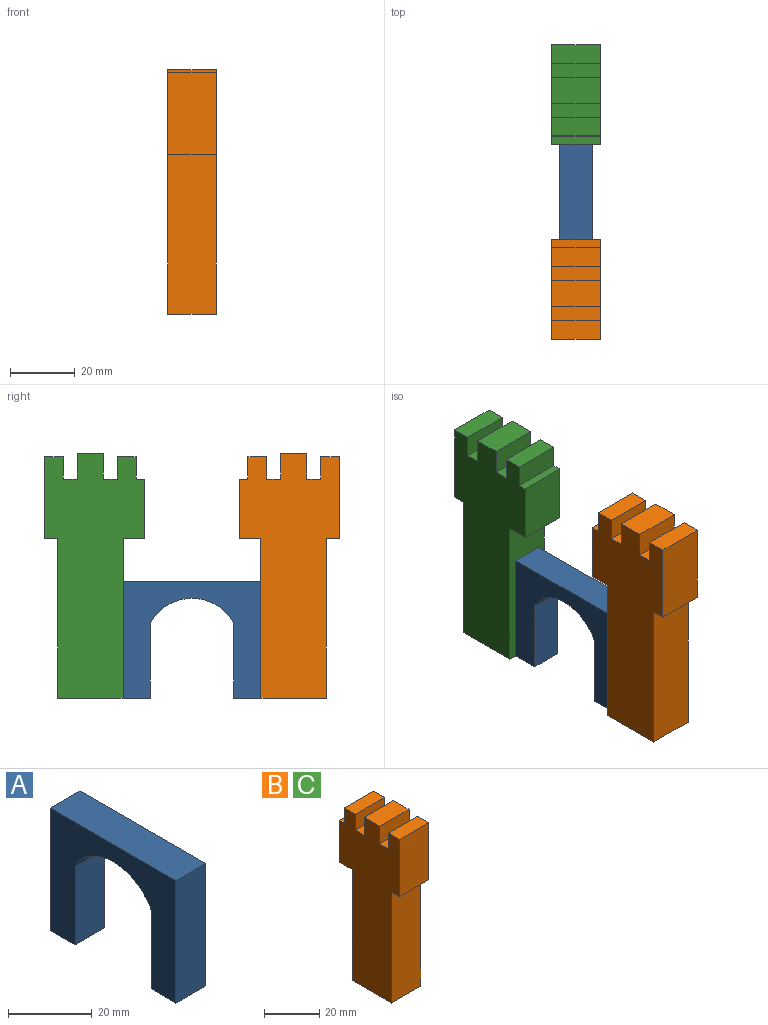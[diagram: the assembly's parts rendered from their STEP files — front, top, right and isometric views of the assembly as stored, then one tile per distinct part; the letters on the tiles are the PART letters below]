
ASSEMBLY  parts=3 mates=2
PART A: 10 faces, bbox 10x42.5x35.9 mm
  f0: plane 22.96x10mm, normal (0,-1,0), area 229.6mm2, adj f1,f7,f8,f9
  f1: plane 10x8.32mm, normal (0,0,-1), area 83.2mm2, adj f0,f2,f8,f9
  f2: plane 35.88x10mm, normal (0,1,0), area 358.8mm2, adj f1,f3,f8,f9
  f3: plane 42.48x10mm, normal (0,0,1), area 424.8mm2, adj f2,f4,f8,f9
  f4: plane 35.88x10mm, normal (0,-1,0), area 358.8mm2, adj f3,f5,f8,f9
  f5: plane 10x8.32mm, normal (0,0,-1), area 83.2mm2, adj f4,f6,f8,f9
  f6: plane 22.96x10mm, normal (0,1,0), area 229.6mm2, adj f5,f7,f8,f9
  f7: cylinder r=14.61mm len=25.83mm, axis (-1,0,0), area 316.8mm2, adj f0,f6,f8,f9
  f8: plane 42.48x35.88mm, normal (1,0,0), area 787.8mm2, adj f0,f1,f2,f3,f4,f5,f6,f7
  f9: plane 42.48x35.88mm, normal (-1,0,0), area 787.8mm2, adj f0,f1,f2,f3,f4,f5,f6,f7
PART B: 20 faces, bbox 15x30.7x75.2 mm
  f0: plane 49.08x15mm, normal (0,1,0), area 736.2mm2, adj f1,f17,f18,f19
  f1: plane 15x6.6mm, normal (0,0,-1), area 99mm2, adj f0,f2,f18,f19
  f2: plane 18.37x15mm, normal (0,1,0), area 275.5mm2, adj f1,f3,f18,f19
  f3: plane 15x2.58mm, normal (0,0,1), area 38.7mm2, adj f2,f4,f18,f19
  f4: plane 15x6.89mm, normal (0,1,0), area 103.3mm2, adj f3,f5,f18,f19
  f5: plane 15x5.74mm, normal (0,0,1), area 86.1mm2, adj f4,f6,f18,f19
  f6: plane 15x6.89mm, normal (0,-1,0), area 103.3mm2, adj f5,f7,f18,f19
  f7: plane 15x4.31mm, normal (0,0,1), area 64.6mm2, adj f6,f8,f18,f19
  f8: plane 15x7.75mm, normal (0,1,0), area 116.2mm2, adj f7,f9,f18,f19
  f9: plane 15x8.04mm, normal (0,0,1), area 120.6mm2, adj f8,f10,f18,f19
  f10: plane 15x7.75mm, normal (0,-1,0), area 116.2mm2, adj f9,f11,f18,f19
  f11: plane 15x4.31mm, normal (0,0,1), area 64.6mm2, adj f10,f12,f18,f19
  f12: plane 15x6.89mm, normal (0,1,0), area 103.3mm2, adj f11,f13,f18,f19
  f13: plane 15x5.74mm, normal (0,0,1), area 86.1mm2, adj f12,f14,f18,f19
  f14: plane 25.26x15mm, normal (0,-1,0), area 378.9mm2, adj f13,f15,f18,f19
  f15: plane 15x4.02mm, normal (0,0,-1), area 60.3mm2, adj f14,f16,f18,f19
  f16: plane 49.08x15mm, normal (0,-1,0), area 736.2mm2, adj f15,f17,f18,f19
  f17: plane 20.09x15mm, normal (0,0,-1), area 301.4mm2, adj f0,f16,f18,f19
  f18: plane 75.2x30.71mm, normal (1,0,0), area 1691.7mm2, adj f0,f1,f2,f3,f4,f5,f6,f7
  f19: plane 75.2x30.71mm, normal (-1,0,0), area 1691.7mm2, adj f0,f1,f2,f3,f4,f5,f6,f7
PART C: same geometry as B
PLACE A t=(-5,12.63,59.69)mm
PLACE B t=(0,0,2)mm
PLACE C rot(axis=(0,0,1),180deg) t=(0,-165.04,2)mm
MATE fastened C.f0 <-> A.f2  axis (0,-1,0) through (0,-61.28,-5.89)mm
MATE fastened B.f0 <-> A.f4  axis (0,1,0) through (0,-103.76,-5.89)mm
